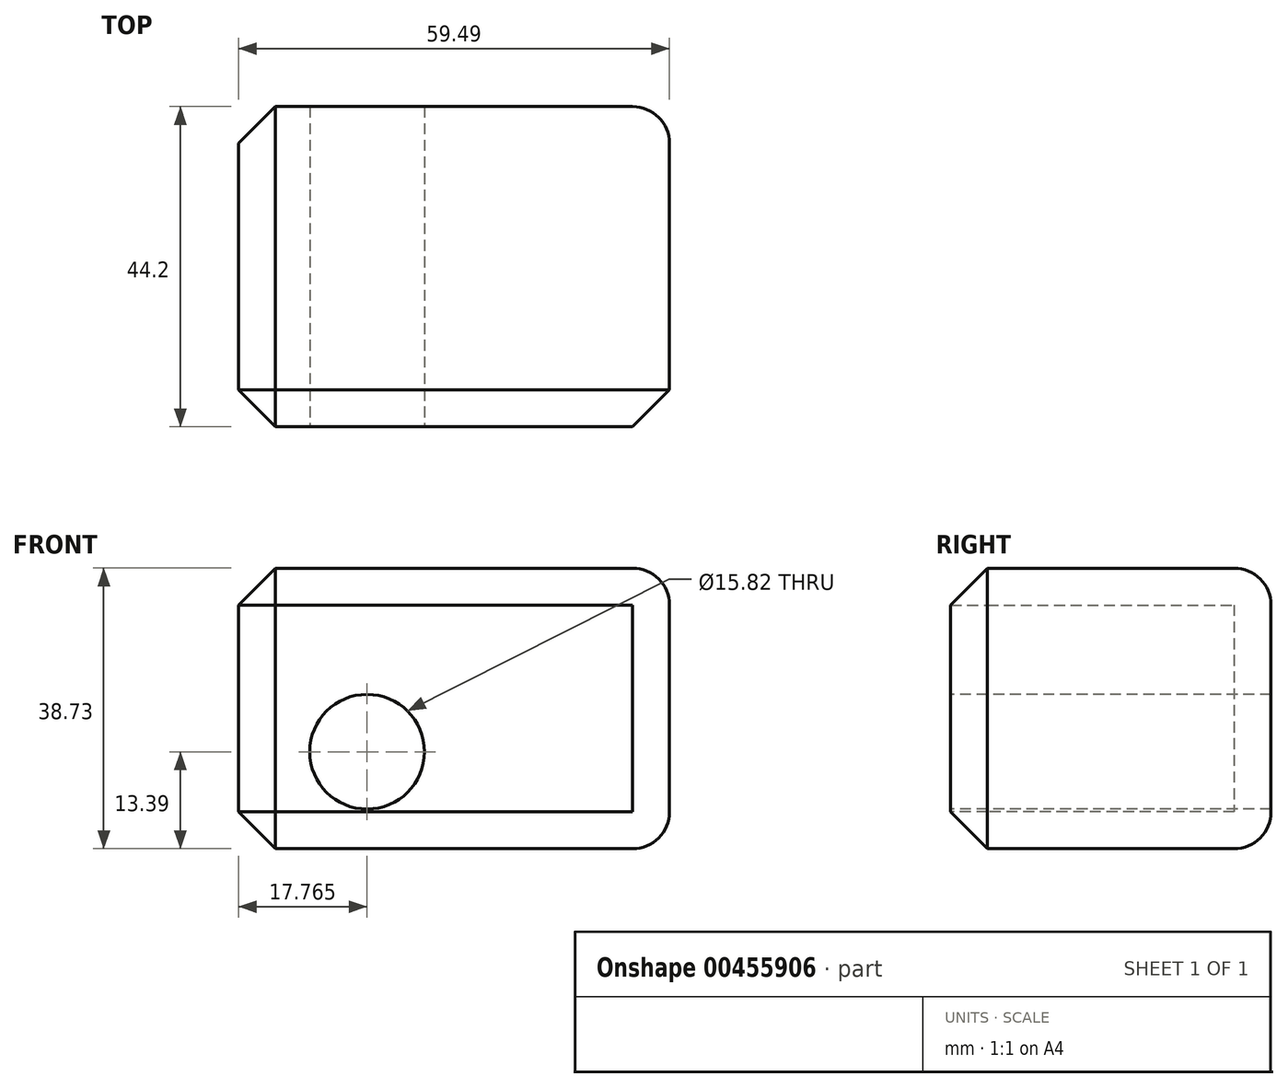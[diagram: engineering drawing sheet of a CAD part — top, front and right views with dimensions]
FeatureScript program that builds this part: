
annotation { "Feature Type Name" : "Feature", "Feature Type Description" : "" }
export const myFeature = defineFeature(function(context is Context, id is Id, definition is map)
    precondition{}
    {
        {
            var Q0;
            Q0=qCreatedBy(makeId("Front.planeOp"),FACE);
            var sketch = newSketch(context, id + "F0", { "sketchPlane" : qUnion([Q0])});
            skLineSegment(sketch, "E0.bottom", {"start": v(0, 0) * mm, "end": v(59.49, 0) * mm});
            skLineSegment(sketch, "E0.top", {"start": v(0, 38.73) * mm, "end": v(59.49, 38.73) * mm});
            skLineSegment(sketch, "E0.left", {"start": v(0, 0) * mm, "end": v(0, 38.73) * mm});
            skLineSegment(sketch, "E0.right", {"start": v(59.49, 0) * mm, "end": v(59.49, 38.73) * mm});
            skSolve(sketch);
        }
        {
            var Q0;
            Q0 = qSketchRegion(id + "F0", true);
            extrude(context, id + "F1", {"entities" : qUnion([Q0]), "depth" : 44.2 * mm});
        }
        {
            var Q0;
            Q0=makeQuery(id+"F1.opExtrude","CAP_FACE",FACE,{"disambiguationData":[OSD([sQuery(id+"F0.wireOp",EDGE,"E0.bottom"),sQuery(id+"F0.wireOp",EDGE,"E0.top"),sQuery(id+"F0.wireOp",EDGE,"E0.left"),sQuery(id+"F0.wireOp",EDGE,"E0.right")])],"isStart":false});
            var sketch = newSketch(context, id + "F2", { "sketchPlane" : qUnion([Q0])});
            skCircle(sketch, "E1", {"center": v(17.76, 13.39) * mm, "radius": 7.91 * mm});
            skSolve(sketch);
        }
        {
            var Q0;
            Q0 = qSketchRegion(id + "F2", true);
            extrude(context, id + "F3", {"entities" : qUnion([Q0]), "operationType" : NewBodyOperationType.REMOVE, "oppositeDirection" : true, "depth" : 70.1 * mm});
        }
        {
            var Q0;
            Q0=makeQuery(id+"F1.opExtrude","SWEPT_EDGE",EDGE,{"disambiguationData":[OSD([sQuery(id+"F0.wireOp",EDGE,"E0.top"),sQuery(id+"F0.wireOp",EDGE,"E0.right")])]});
            var Q1;
            Q1=makeQuery(id+"F1.opExtrude","SWEPT_EDGE",EDGE,{"disambiguationData":[OSD([sQuery(id+"F0.wireOp",EDGE,"E0.bottom"),sQuery(id+"F0.wireOp",EDGE,"E0.right")])]});
            var Q2;
            Q2=makeQuery(id+"F1.opExtrude","CAP_EDGE",EDGE,{"disambiguationData":[OSD([sQuery(id+"F0.wireOp",EDGE,"E0.right")])],"isStart":true});
            var Q3;
            Q3=makeQuery(id+"F1.opExtrude","CAP_EDGE",EDGE,{"disambiguationData":[OSD([sQuery(id+"F0.wireOp",EDGE,"E0.top")])],"isStart":true});
            var Q4;
            Q4=makeQuery(id+"F1.opExtrude","CAP_EDGE",EDGE,{"disambiguationData":[OSD([sQuery(id+"F0.wireOp",EDGE,"E0.bottom")])],"isStart":true});
            fillet(context, id + "F4", {"entities" : qUnion([Q0, Q1, Q2, Q3, Q4]), "radius" : 5.08 * mm, "tangentPropagation" : true, "allowEdgeOverflow" : false});
        }
        {
            var Q0;
            Q0=makeQuery(id+"F1.opExtrude","CAP_EDGE",EDGE,{"disambiguationData":[OSD([sQuery(id+"F0.wireOp",EDGE,"E0.left")])],"isStart":false});
            var Q1;
            Q1=makeQuery(id+"F1.opExtrude","CAP_EDGE",EDGE,{"disambiguationData":[OSD([sQuery(id+"F0.wireOp",EDGE,"E0.bottom")])],"isStart":false});
            var Q2;
            Q2=makeQuery(id+"F1.opExtrude","SWEPT_EDGE",EDGE,{"disambiguationData":[OSD([sQuery(id+"F0.wireOp",EDGE,"E0.bottom"),sQuery(id+"F0.wireOp",EDGE,"E0.left")])]});
            chamfer(context, id + "F5", {"entities" : qUnion([Q0, Q1, Q2]), "width" : 5.08 * mm, "tangentPropagation" : true});
        }
    });
